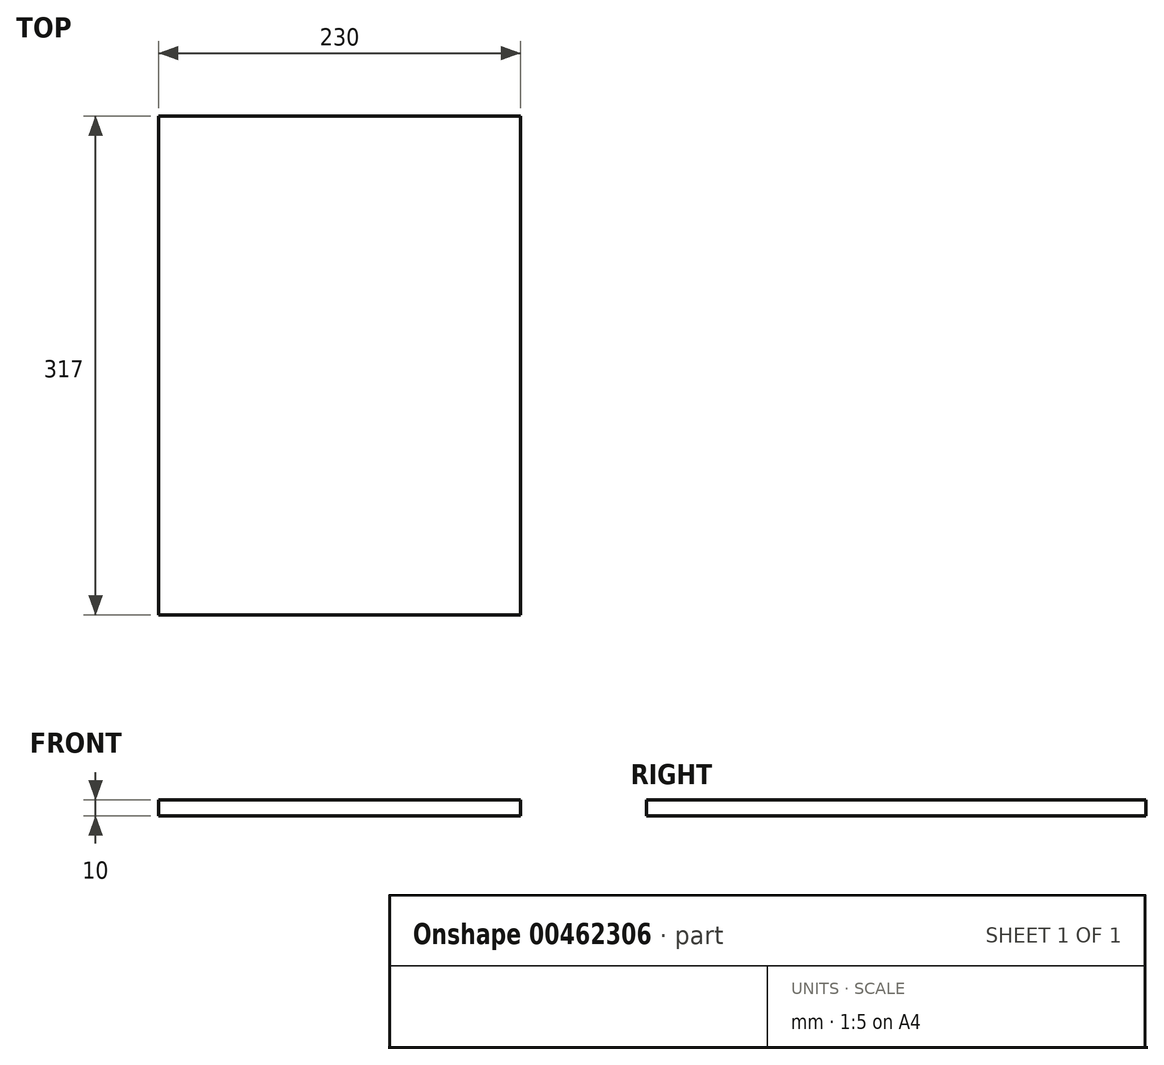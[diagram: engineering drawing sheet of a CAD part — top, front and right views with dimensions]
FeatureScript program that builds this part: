
annotation { "Feature Type Name" : "Feature", "Feature Type Description" : "" }
export const myFeature = defineFeature(function(context is Context, id is Id, definition is map)
    precondition{}
    {
        {
            var Q0;
            Q0=qCreatedBy(makeId("Top.planeOp"),FACE);
            var sketch = newSketch(context, id + "F0", { "sketchPlane" : qUnion([Q0])});
            skLineSegment(sketch, "E0.bottom", {"start": v(115, 158.5) * mm, "end": v(-115, 158.5) * mm});
            skLineSegment(sketch, "E0.top", {"start": v(115, -158.5) * mm, "end": v(-115, -158.5) * mm});
            skLineSegment(sketch, "E0.left", {"start": v(115, 158.5) * mm, "end": v(115, -158.5) * mm});
            skLineSegment(sketch, "E0.right", {"start": v(-115, 158.5) * mm, "end": v(-115, -158.5) * mm});
            skPoint(sketch, "E0.middle", {"position": v(0, 0) * mm});
            skLineSegment(sketch, "E1.bottom", {"start": v(105, 148.5) * mm, "end": v(-105, 148.5) * mm, "construction": true});
            skLineSegment(sketch, "E1.top", {"start": v(105, -148.5) * mm, "end": v(-105, -148.5) * mm, "construction": true});
            skLineSegment(sketch, "E1.left", {"start": v(105, 148.5) * mm, "end": v(105, -148.5) * mm, "construction": true});
            skLineSegment(sketch, "E1.right", {"start": v(-105, 148.5) * mm, "end": v(-105, -148.5) * mm, "construction": true});
            skCircle(sketch, "E2", {"center": v(105, 148.5) * mm, "radius": 10 * mm, "construction": true});
            skSolve(sketch);
        }
        {
            var Q0;
            Q0 = qSketchRegion(id + "F0", true);
            extrude(context, id + "F1", {"entities" : qUnion([Q0]), "oppositeDirection" : true, "depth" : 10 * mm});
        }
    });
